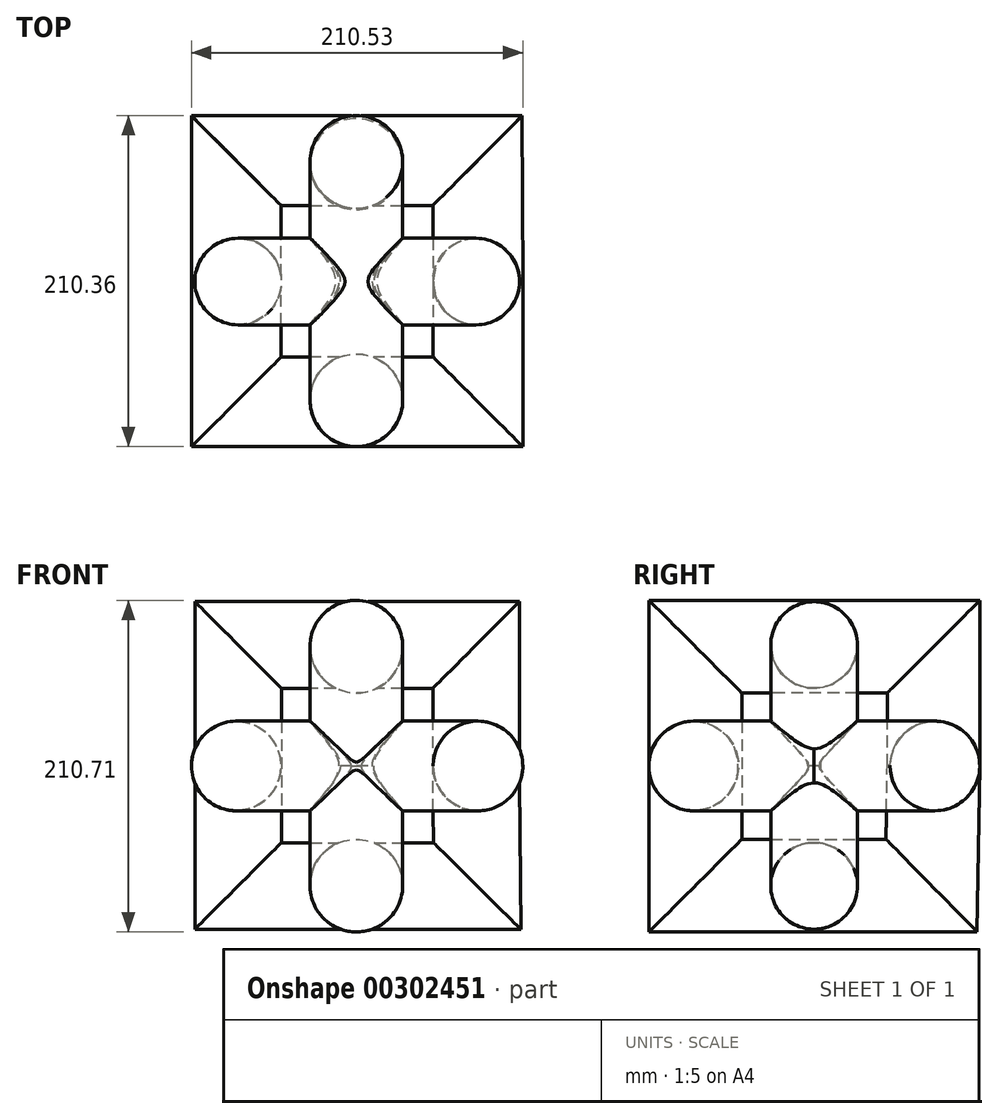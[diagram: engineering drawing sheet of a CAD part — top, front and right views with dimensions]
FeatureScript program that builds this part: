
annotation { "Feature Type Name" : "Feature", "Feature Type Description" : "" }
export const myFeature = defineFeature(function(context is Context, id is Id, definition is map)
    precondition{}
    {
        {
            var Q0;
            Q0=qCreatedBy(makeId("Top.planeOp"),FACE);
            var sketch = newSketch(context, id + "F0", { "sketchPlane" : qUnion([Q0])});
            skCircle(sketch, "E0", {"center": v(76.06, 0) * mm, "radius": 27.5 * mm});
            skSolve(sketch);
        }
        {
            var Q0;
            Q0=qCreatedBy(makeId("Front.planeOp"),FACE);
            var sketch = newSketch(context, id + "F1", { "sketchPlane" : qUnion([Q0])});
            skLineSegment(sketch, "E1", {"start": v(76.38, 0) * mm, "end": v(76.38, 77.19) * mm});
            skLineSegment(sketch, "E2", {"start": v(76.38, 77.19) * mm, "end": v(-75.4, 77.19) * mm});
            skLineSegment(sketch, "E3", {"start": v(-75.4, 77.19) * mm, "end": v(-75.4, -76.54) * mm});
            skLineSegment(sketch, "E4", {"start": v(-75.4, -76.54) * mm, "end": v(77.03, -76.54) * mm});
            skLineSegment(sketch, "E5", {"start": v(77.03, -76.54) * mm, "end": v(76.38, 0) * mm});
            skSolve(sketch);
        }
        {
            var Q0;
            Q0=makeQuery(id+"F0.imprint","IMPRINT",FACE,{"disambiguationData":[TD([[makeQuery(id+"F0.imprint","IMPRINT",EDGE,{"derivedFrom":sQuery(id+"F0.wireOp",EDGE,"E0")}),1.0]])]});
            var Q1;
            Q1=sQuery(id+"F1.wireOp",EDGE,"E1");
            var Q2;
            Q2=sQuery(id+"F1.wireOp",EDGE,"E2");
            var Q3;
            Q3=sQuery(id+"F1.wireOp",EDGE,"E3");
            var Q4;
            Q4=sQuery(id+"F1.wireOp",EDGE,"E4");
            var Q5;
            Q5=sQuery(id+"F1.wireOp",EDGE,"E5");
            sweep(context, id + "F2", {"profiles" : qUnion([Q0]), "path" : qUnion([Q1, Q2, Q3, Q4, Q5])});
        }
        {
            var Q0;
            Q0=qCreatedBy(makeId("Top.planeOp"),FACE);
            var sketch = newSketch(context, id + "F3", { "sketchPlane" : qUnion([Q0])});
            skLineSegment(sketch, "E6", {"start": v(77.19, 0) * mm, "end": v(77.19, -76.38) * mm});
            skLineSegment(sketch, "E7", {"start": v(77.19, -76.38) * mm, "end": v(-76.22, -76.38) * mm});
            skLineSegment(sketch, "E8", {"start": v(-76.22, -76.38) * mm, "end": v(-76.22, 0) * mm});
            skLineSegment(sketch, "E9", {"start": v(-76.22, 0) * mm, "end": v(-76.22, 76.7) * mm});
            skLineSegment(sketch, "E10", {"start": v(-76.22, 76.7) * mm, "end": v(0, 76.7) * mm});
            skLineSegment(sketch, "E11", {"start": v(0, 76.7) * mm, "end": v(76.87, 76.7) * mm});
            skLineSegment(sketch, "E12", {"start": v(76.87, 76.7) * mm, "end": v(77.19, 0) * mm});
            skSolve(sketch);
        }
        {
            var Q0;
            Q0=qCreatedBy(makeId("Front.planeOp"),FACE);
            var sketch = newSketch(context, id + "F4", { "sketchPlane" : qUnion([Q0])});
            skCircle(sketch, "E13", {"center": v(77.26, 0) * mm, "radius": 28.49 * mm});
            skSolve(sketch);
        }
        {
            var Q0;
            Q0=makeQuery(id+"F4.imprint","IMPRINT",FACE,{"disambiguationData":[TD([[makeQuery(id+"F4.imprint","IMPRINT",EDGE,{"derivedFrom":sQuery(id+"F4.wireOp",EDGE,"E13")}),1.0]])]});
            var Q1;
            Q1=sQuery(id+"F3.wireOp",EDGE,"E6");
            var Q2;
            Q2=sQuery(id+"F3.wireOp",EDGE,"E7");
            var Q3;
            Q3=sQuery(id+"F3.wireOp",EDGE,"E8");
            var Q4;
            Q4=sQuery(id+"F3.wireOp",EDGE,"E9");
            var Q5;
            Q5=sQuery(id+"F3.wireOp",EDGE,"E10");
            var Q6;
            Q6=sQuery(id+"F3.wireOp",EDGE,"E11");
            var Q7;
            Q7=sQuery(id+"F3.wireOp",EDGE,"E12");
            sweep(context, id + "F5", {"operationType" : NewBodyOperationType.ADD, "profiles" : qUnion([Q0]), "path" : qUnion([Q1, Q2, Q3, Q4, Q5, Q6, Q7])});
        }
        {
            var Q0;
            Q0=qCreatedBy(makeId("Top.planeOp"),FACE);
            var sketch = newSketch(context, id + "F6", { "sketchPlane" : qUnion([Q0])});
            skCircle(sketch, "E14", {"center": v(0, 75.96) * mm, "radius": 29.46 * mm});
            skSolve(sketch);
        }
        {
            var Q0;
            Q0=qCreatedBy(makeId("Right.planeOp"),FACE);
            var sketch = newSketch(context, id + "F7", { "sketchPlane" : qUnion([Q0])});
            skLineSegment(sketch, "E15", {"start": v(76.64, 0) * mm, "end": v(76.64, 76.5) * mm});
            skLineSegment(sketch, "E16", {"start": v(76.64, 76.5) * mm, "end": v(-76.06, 76.5) * mm});
            skLineSegment(sketch, "E17", {"start": v(-76.06, 76.5) * mm, "end": v(-76.06, -76.65) * mm});
            skLineSegment(sketch, "E18", {"start": v(-76.06, -76.65) * mm, "end": v(75.29, -76.65) * mm});
            skLineSegment(sketch, "E19", {"start": v(75.29, -76.65) * mm, "end": v(76.64, 0) * mm});
            skSolve(sketch);
        }
        {
            var Q0;
            Q0=makeQuery(id+"F6.imprint","IMPRINT",FACE,{"disambiguationData":[TD([[makeQuery(id+"F6.imprint","IMPRINT",EDGE,{"derivedFrom":sQuery(id+"F6.wireOp",EDGE,"E14")}),1.0]])]});
            var Q1;
            Q1=sQuery(id+"F7.wireOp",EDGE,"E15");
            var Q2;
            Q2=sQuery(id+"F7.wireOp",EDGE,"E16");
            var Q3;
            Q3=sQuery(id+"F7.wireOp",EDGE,"E17");
            var Q4;
            Q4=sQuery(id+"F7.wireOp",EDGE,"E18");
            var Q5;
            Q5=sQuery(id+"F7.wireOp",EDGE,"E19");
            sweep(context, id + "F8", {"operationType" : NewBodyOperationType.ADD, "profiles" : qUnion([Q0]), "path" : qUnion([Q1, Q2, Q3, Q4, Q5])});
        }
    });
